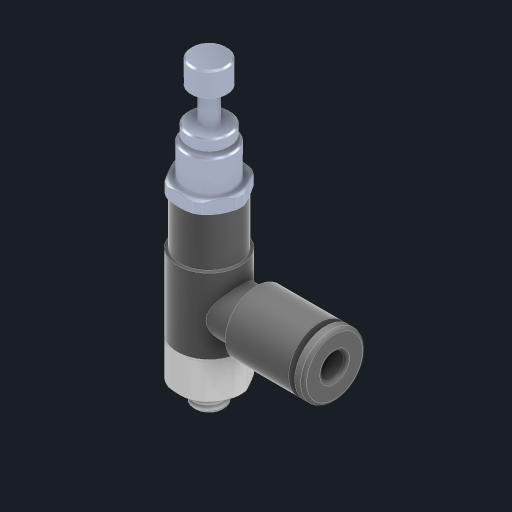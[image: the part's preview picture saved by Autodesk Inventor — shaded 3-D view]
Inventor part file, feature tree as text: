
AUTODESK INVENTOR PART (.ipt)
format: ipt  version: 2023 (Build 270158030, 158C)  size: 283,648 bytes
history: mixed  units: in
note: dims shown in document units (in); Inventor stores cm internally (conversion verified against a paired STEP export)
features: thread x1, other x1, imported_body x1
ambient origin geometry x8: Origin, YZ Plane, XZ Plane, XY Plane, X Axis, Y Axis, Z Axis, Center Point
bodies: Solid1 (imported_parasolid)
feature tree (3):
  thread  "Thread1"  [1 undecoded]
  other  "Cham"
  imported_body  NMx_Import_Brep_tag  [imported B-rep: ~8 faces, bbox_mm=[0.0, 0.0, 0.0]]
note: 1 required parameter value undecoded (feature->parameter linkage not recoverable at this tier; creation-order binding heuristic only, values carry confidence <= 0.55)
